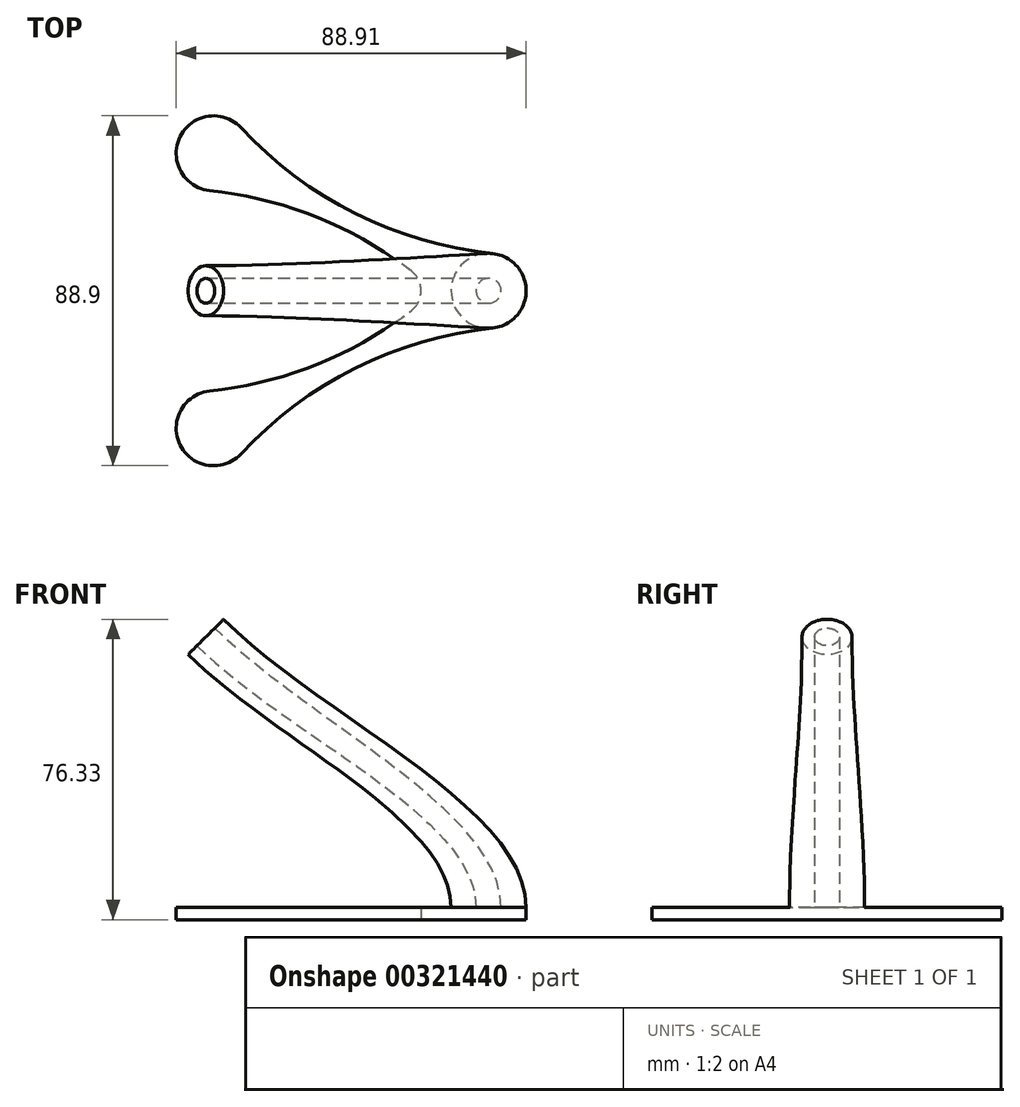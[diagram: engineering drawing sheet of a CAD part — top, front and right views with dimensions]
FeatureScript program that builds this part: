
annotation { "Feature Type Name" : "Feature", "Feature Type Description" : "" }
export const myFeature = defineFeature(function(context is Context, id is Id, definition is map)
    precondition{}
    {
        {
            var Q0;
            Q0=qCreatedBy(makeId("Top.planeOp"),FACE);
            var sketch = newSketch(context, id + "F0", { "sketchPlane" : qUnion([Q0])});
            skArc(sketch, "E0", {"start": v(1, -9.47) * mm, "mid": v(9.53, 0) * mm, "end": v(1, 9.47) * mm});
            skArc(sketch, "E1", {"start": v(-62.87, 41.4) * mm, "mid": v(-78.37, 39.18) * mm, "end": v(-70.84, 25.45) * mm});
            skArc(sketch, "E2", {"start": v(-70.84, -25.45) * mm, "mid": v(-78.37, -39.18) * mm, "end": v(-62.87, -41.4) * mm});
            skLineSegment(sketch, "E3", {"start": v(0, 0) * mm, "end": v(-69.85, 34.93) * mm, "construction": true});
            skLineSegment(sketch, "E4", {"start": v(-69.85, -34.93) * mm, "end": v(-69.85, 34.93) * mm, "construction": true});
            skLineSegment(sketch, "E5", {"start": v(-69.85, -34.93) * mm, "end": v(0, 0) * mm, "construction": true});
            skArc(sketch, "E6", {"start": v(-19.64, 5.04) * mm, "mid": v(-43.83, 18.79) * mm, "end": v(-70.84, 25.45) * mm});
            skArc(sketch, "E7", {"start": v(-62.87, 41.4) * mm, "mid": v(-33.83, 19.64) * mm, "end": v(1, 9.47) * mm});
            skLineSegment(sketch, "E8", {"start": v(-69.85, 0) * mm, "end": v(0, 0) * mm, "construction": true});
            skArc(sketch, "E9", {"start": v(-70.84, -25.45) * mm, "mid": v(-43.83, -18.79) * mm, "end": v(-19.64, -5.04) * mm});
            skArc(sketch, "E10", {"start": v(1, -9.47) * mm, "mid": v(-33.83, -19.64) * mm, "end": v(-62.87, -41.4) * mm});
            skPoint(sketch, "E11.visualSharp", {"position": v(-13.57, 0) * mm});
            skArc(sketch, "E11.filletArc", {"start": v(-19.64, -5.04) * mm, "mid": v(-17.15, 0) * mm, "end": v(-19.64, 5.04) * mm});
            skSolve(sketch);
        }
        {
            var Q0;
            Q0 = qSketchRegion(id + "F0", true);
            extrude(context, id + "F1", {"entities" : qUnion([Q0]), "depth" : 3.17 * mm});
        }
        {
            var Q0;
            Q0=qCreatedBy(makeId("Front.planeOp"),FACE);
            var sketch = newSketch(context, id + "F2", { "sketchPlane" : qUnion([Q0])});
            skLineSegment(sketch, "E12", {"start": v(0, 0) * mm, "end": v(-71.84, 71.84) * mm, "construction": true});
            skSolve(sketch);
        }
        {
            var Q0;
            Q0=sQuery(id+"F2.wireOp",VERTEX,"E12.end");
            var Q1;
            Q1=sQuery(id+"F2.wireOp",EDGE,"E12");
            cPlane(context, id + "F3", {"entities" : qUnion([Q0, Q1]), "cplaneType" : CPlaneType.LINE_POINT, "offset" : 25.4 * mm, "width" : 152.4 * mm, "height" : 152.4 * mm});
        }
        {
            var Q0;
            Q0=qCreatedBy(id+"F3.planeOp",FACE);
            var sketch = newSketch(context, id + "F4", { "sketchPlane" : qUnion([Q0])});
            skCircle(sketch, "E13", {"center": v(0, 0) * mm, "radius": 6.35 * mm});
            skSolve(sketch);
        }
        {
            var Q0;
            Q0=makeQuery(id+"F1.opExtrude","CAP_FACE",FACE,{"disambiguationData":[OSD([sQuery(id+"F0.wireOp",EDGE,"E0"),sQuery(id+"F0.wireOp",EDGE,"E1"),sQuery(id+"F0.wireOp",EDGE,"E2"),sQuery(id+"F0.wireOp",EDGE,"E6"),sQuery(id+"F0.wireOp",EDGE,"E7"),sQuery(id+"F0.wireOp",EDGE,"E9"),sQuery(id+"F0.wireOp",EDGE,"E10"),sQuery(id+"F0.wireOp",EDGE,"E11.filletArc")])],"isStart":false});
            var sketch = newSketch(context, id + "F5", { "sketchPlane" : qUnion([Q0])});
            skCircle(sketch, "E14", {"center": v(0, 0) * mm, "radius": 9.53 * mm});
            skSolve(sketch);
        }
        {
            var Q1;
            Q1 = qSketchRegion(id + "F5", true);
            var Q2;
            Q2=makeQuery(id+"F4.imprint","IMPRINT",FACE,{"disambiguationData":[TD([[makeQuery(id+"F4.imprint","IMPRINT",EDGE,{"derivedFrom":sQuery(id+"F4.wireOp",EDGE,"E13")}),1.0]])]});
            loft(context, id + "F6", {"operationType" : NewBodyOperationType.ADD, "startCondition" : LoftEndDerivativeType.NORMAL_TO_PROFILE, "startMagnitude" : 1, "endCondition" : LoftEndDerivativeType.NORMAL_TO_PROFILE, "endMagnitude" : 1, "sheetProfilesArray" : [{ "sheetProfileEntities" : qUnion([Q1]) }, { "sheetProfileEntities" : qUnion([Q2]) }]});
        }
        {
            var Q0;
            Q0=qCreatedBy(id+"F3.planeOp",FACE);
            var sketch = newSketch(context, id + "F7", { "sketchPlane" : qUnion([Q0])});
            skCircle(sketch, "E15", {"center": v(0, 0) * mm, "radius": 3.18 * mm});
            skSolve(sketch);
        }
        {
            var Q0;
            Q0=makeQuery(id+"F1.opExtrude","CAP_FACE",FACE,{"disambiguationData":[OSD([sQuery(id+"F0.wireOp",EDGE,"E0"),sQuery(id+"F0.wireOp",EDGE,"E1"),sQuery(id+"F0.wireOp",EDGE,"E2"),sQuery(id+"F0.wireOp",EDGE,"E6"),sQuery(id+"F0.wireOp",EDGE,"E7"),sQuery(id+"F0.wireOp",EDGE,"E9"),sQuery(id+"F0.wireOp",EDGE,"E10"),sQuery(id+"F0.wireOp",EDGE,"E11.filletArc")])],"isStart":false});
            var sketch = newSketch(context, id + "F8", { "sketchPlane" : qUnion([Q0])});
            skCircle(sketch, "E16", {"center": v(0, 0) * mm, "radius": 3.18 * mm});
            skSolve(sketch);
        }
        {
            var Q1;
            Q1 = qSketchRegion(id + "F8", true);
            var Q2;
            Q2 = qSketchRegion(id + "F7", true);
            loft(context, id + "F9", {"operationType" : NewBodyOperationType.REMOVE, "startCondition" : LoftEndDerivativeType.NORMAL_TO_PROFILE, "startMagnitude" : 1, "endCondition" : LoftEndDerivativeType.NORMAL_TO_PROFILE, "endMagnitude" : 1, "sheetProfilesArray" : [{ "sheetProfileEntities" : qUnion([Q1]) }, { "sheetProfileEntities" : qUnion([Q2]) }]});
        }
    });
